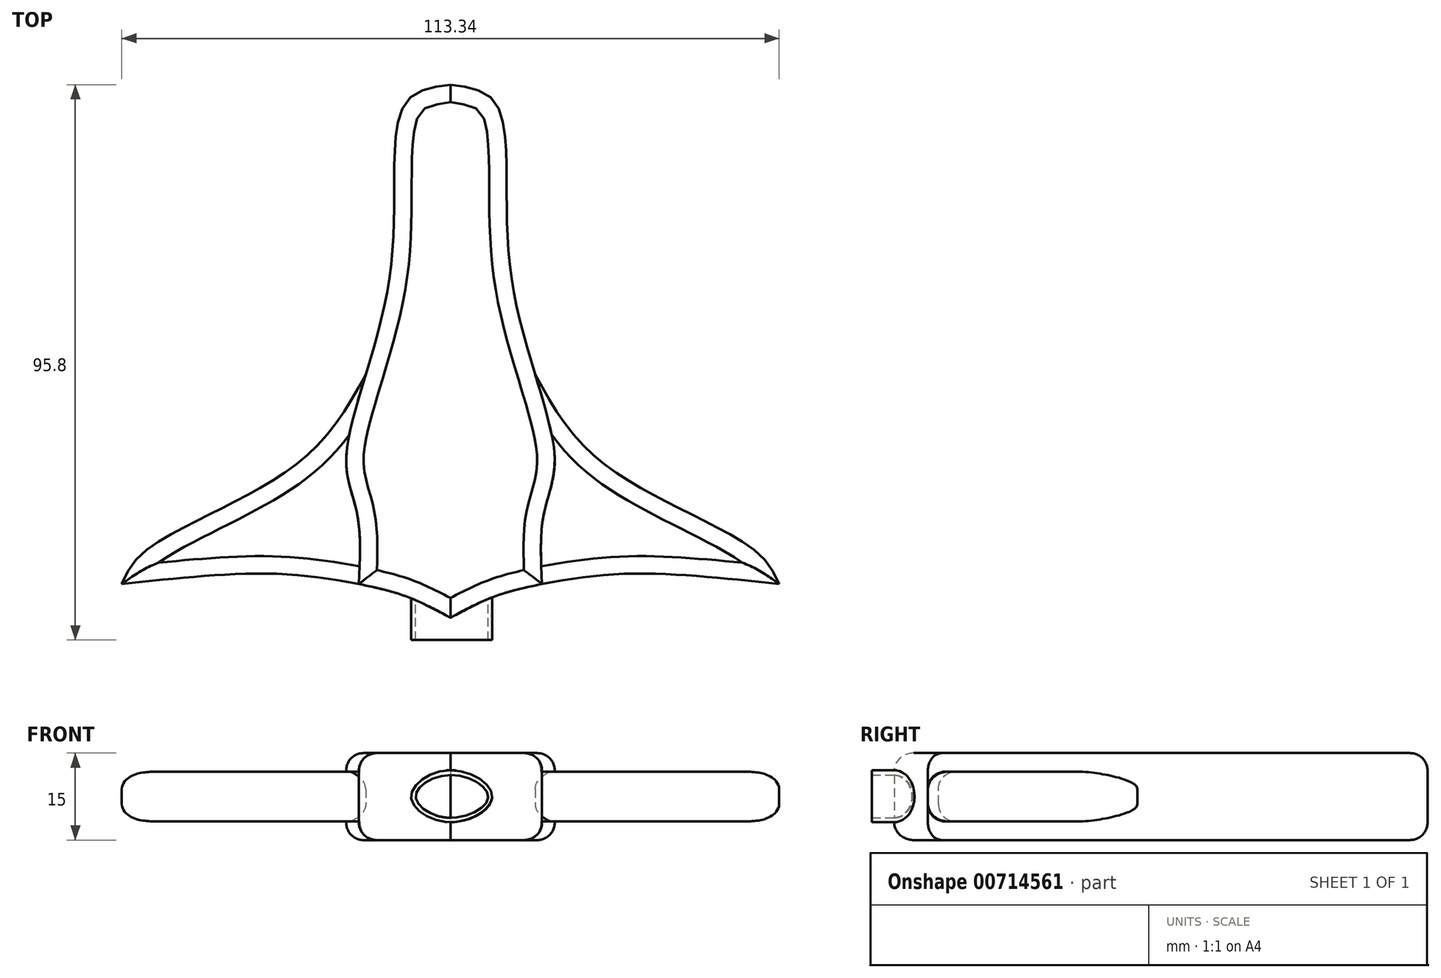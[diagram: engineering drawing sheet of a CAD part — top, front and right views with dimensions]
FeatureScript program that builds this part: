
annotation { "Feature Type Name" : "Feature", "Feature Type Description" : "" }
export const myFeature = defineFeature(function(context is Context, id is Id, definition is map)
    precondition{}
    {
        {
            var Q0;
            Q0=qCreatedBy(makeId("Top.planeOp"),FACE);
            var sketch = newSketch(context, id + "F0", { "sketchPlane" : qUnion([Q0])});
            skLineSegment(sketch, "E0", {"start": v(0, 0) * mm, "end": v(0, 50) * mm});
            skFitSpline(sketch, "E1", {"points": [v(0, 50) * mm, v(-7.9, 46.63) * mm, v(-10.34, 17.9) * mm, v(-17.96, -14) * mm, v(-16.09, -24.06) * mm, v(-15.8, -36.13) * mm], "startDerivative": vector(-66.4, -8.16) * mm, "endDerivative": vector(-3.75, -76.11) * mm});
            skFitSpline(sketch, "E2", {"points": [v(-14.6, 0) * mm, v(-27, -15.8) * mm, v(-52.4, -30.27) * mm, v(-56.67, -36.13) * mm], "startDerivative": vector(-25.46, -46.53) * mm, "endDerivative": vector(-11.55, -26.78) * mm});
            skFitSpline(sketch, "E3", {"points": [v(-56.67, -36.13) * mm, v(-30.52, -34.35) * mm, v(-15.8, -36.13) * mm], "startDerivative": vector(49.1, 5.2) * mm, "endDerivative": vector(31.82, -5.71) * mm});
            skFitSpline(sketch, "E4", {"points": [v(-15.8, -36.13) * mm, v(-7.71, -38.25) * mm, v(0, -41.95) * mm], "startDerivative": vector(16.5, -3.47) * mm, "endDerivative": vector(15.1, -8.16) * mm});
            skLineSegment(sketch, "E5", {"start": v(0, -41.95) * mm, "end": v(0, 0) * mm});
            skSolve(sketch);
        }
        {
            var Q0;
            {var subQ3=sQuery(id+"F0.wireOp",EDGE,"E0");Q0=makeQuery(id+"F0.imprint","IMPRINT",FACE,{"disambiguationData":[TD([[makeQuery(id+"F0.imprint","IMPRINT",EDGE,{"derivedFrom":subQ3}),1.0]])]});}
            extrude(context, id + "F1", {"entities" : qUnion([Q0]), "depth" : 7.5 * mm, "offsetDistance" : 25 * mm});
        }
        {
            var Q0;
            Q0 = qSketchRegion(id + "F0", true);
            extrude(context, id + "F2", {"entities" : qUnion([Q0]), "operationType" : NewBodyOperationType.ADD, "depth" : 4.3 * mm, "offsetDistance" : 25 * mm});
        }
        {
            var Q0;
            Q0=makeQuery(id+"F1.opExtrude","CAP_EDGE",EDGE,{"disambiguationData":[OSD([sQuery(id+"F0.wireOp",EDGE,"E1")])],"isStart":false});
            var Q1;
            Q1=makeQuery(id+"F2.opExtrude","CAP_EDGE",EDGE,{"disambiguationData":[OSD([sQuery(id+"F0.wireOp",EDGE,"E2")])],"isStart":false});
            var Q2;
            Q2=makeQuery(id+"F2.opExtrude","CAP_EDGE",EDGE,{"disambiguationData":[OSD([sQuery(id+"F0.wireOp",EDGE,"E3")])],"isStart":false});
            var Q3;
            Q3=makeQuery(id+"F1.opExtrude","CAP_EDGE",EDGE,{"disambiguationData":[OSD([sQuery(id+"F0.wireOp",EDGE,"E4")])],"isStart":false});
            fillet(context, id + "F3", {"entities" : qUnion([Q0, Q1, Q2, Q3]), "radius" : 3 * mm, "tangentPropagation" : true, "allowEdgeOverflow" : false});
        }
        {
            var Q0;
            Q0=makeQuery(id+"F1.opExtrude","SWEPT_BODY",BODY,{"disambiguationData":[OSD([sQuery(id+"F0.wireOp",EDGE,"E0"),sQuery(id+"F0.wireOp",EDGE,"E1"),sQuery(id+"F0.wireOp",EDGE,"E4"),sQuery(id+"F0.wireOp",EDGE,"E5")])]});
            var Q1;
            Q1=qCreatedBy(makeId("Right.planeOp"),FACE);
            mirror(context, id + "F4", {"operationType" : NewBodyOperationType.ADD, "entities" : qUnion([Q0]), "mirrorPlane" : qUnion([Q1])});
        }
        {
            var Q0;
            Q0=makeQuery(id+"F1.opExtrude","SWEPT_BODY",BODY,{"disambiguationData":[OSD([sQuery(id+"F0.wireOp",EDGE,"E0"),sQuery(id+"F0.wireOp",EDGE,"E1"),sQuery(id+"F0.wireOp",EDGE,"E4"),sQuery(id+"F0.wireOp",EDGE,"E5")])]});
            var Q1;
            Q1=qCreatedBy(makeId("Top.planeOp"),FACE);
            mirror(context, id + "F5", {"operationType" : NewBodyOperationType.ADD, "entities" : qUnion([Q0]), "mirrorPlane" : qUnion([Q1])});
        }
        {
            var Q0;
            Q0=qCreatedBy(makeId("Front.planeOp"),FACE);
            var sketch = newSketch(context, id + "F6", { "sketchPlane" : qUnion([Q0])});
            skFitSpline(sketch, "E6", {"points": [v(0, 4.55) * mm, v(-6.77, 0) * mm, v(0, -4.42) * mm, v(7.18, 0) * mm, v(0, 4.55) * mm]});
            skFitSpline(sketch, "E7", {"points": [v(0, 3.7) * mm, v(-5.98, 0) * mm, v(0, -3.67) * mm, v(6.52, 0) * mm, v(0, 3.7) * mm]});
            skSolve(sketch);
        }
        {
            var Q0;
            Q0 = qSketchRegion(id + "F6", true);
            extrude(context, id + "F7", {"entities" : qUnion([Q0]), "operationType" : NewBodyOperationType.ADD, "depth" : 45.8 * mm, "offsetDistance" : 25 * mm});
        }
    });
